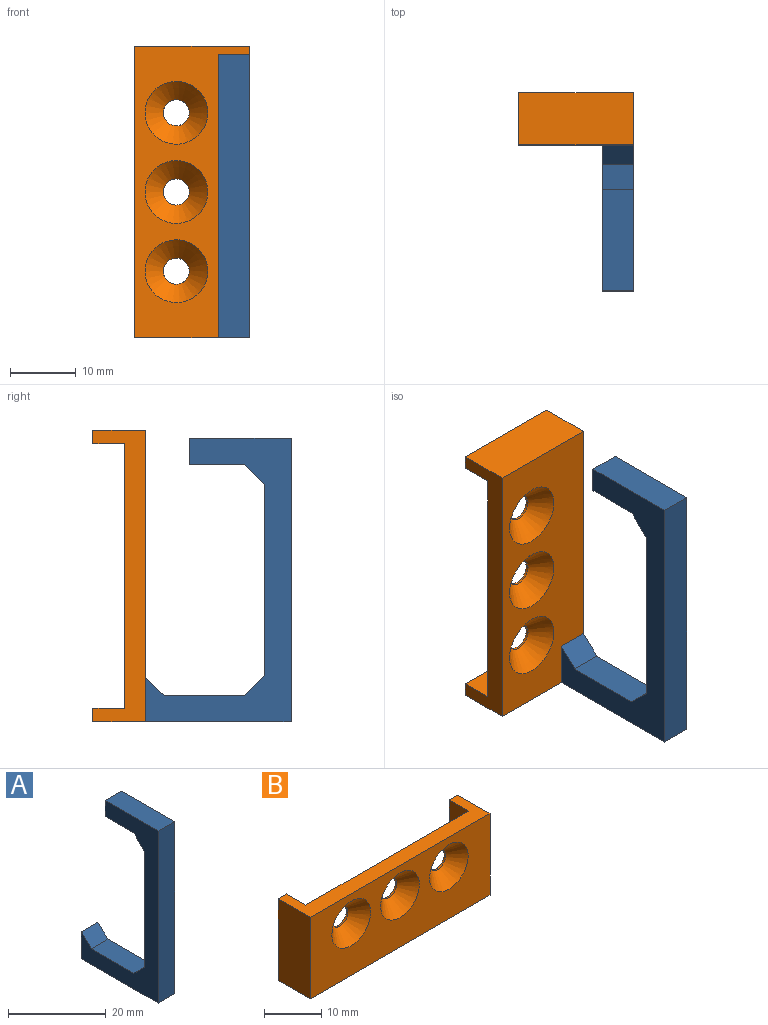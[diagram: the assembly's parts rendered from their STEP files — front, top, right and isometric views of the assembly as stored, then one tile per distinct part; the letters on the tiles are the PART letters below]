
ASSEMBLY  parts=2 mates=1
PART A: 13 faces, bbox 4.8x22.2x43.2 mm
  f0: plane 12.28x4.76mm, normal (0,0,1), area 58.5mm2, adj f1,f9,f10,f12
  f1: plane 4.76x2.93mm, normal (0,-0.69,0.72), area 19.3mm2, adj f0,f2,f9,f10
  f2: plane 6.76x4.76mm, normal (0,1,0), area 32.2mm2, adj f1,f3,f9,f10
  f3: plane 22.23x4.76mm, normal (0,0,-1), area 105.8mm2, adj f2,f4,f9,f10
  f4: plane 43.18x4.76mm, normal (0,-1,0), area 205.6mm2, adj f3,f5,f9,f10
  f5: plane 15.4x4.76mm, normal (0,0,1), area 73.3mm2, adj f4,f6,f9,f10
  f6: plane 4.76x3.97mm, normal (0,1,0), area 18.9mm2, adj f5,f7,f9,f10
  f7: plane 8.38x4.76mm, normal (0,0,-1), area 39.9mm2, adj f6,f9,f10,f11
  f8: plane 29.15x4.76mm, normal (0,1,0), area 138.8mm2, adj f9,f10,f11,f12
  f9: plane 43.18x22.23mm, normal (1,0,0), area 302.6mm2, adj f0,f1,f2,f3,f4,f5,f6,f7
  f10: plane 43.18x22.23mm, normal (-1,0,0), area 302.6mm2, adj f0,f1,f2,f3,f4,f5,f6,f7
  f11: plane 4.76x3.05mm, normal (0,0.71,-0.71), area 20.5mm2, adj f7,f8,f9,f10
  f12: plane 4.76x3.05mm, normal (0,0.71,0.71), area 20.5mm2, adj f0,f8,f9,f10
PART B: 16 faces, bbox 44.5x7.9x17.5 mm
  f0: plane 40.22x17.46mm, normal (0,1,0), area 665.2mm2, adj f1,f7,f8,f9,f10,f11,f12
  f1: plane 17.46x4.76mm, normal (1,0,0), area 83.2mm2, adj f0,f2,f8,f9
  f2: plane 17.46x2.12mm, normal (0,1,0), area 37mm2, adj f1,f3,f8,f9
  f3: plane 17.46x7.94mm, normal (-1,0,0), area 138.6mm2, adj f2,f4,f8,f9
  f4: plane 44.45x17.46mm, normal (0,-1,0), area 561mm2, adj f3,f5,f8,f9,f13,f14,f15
  f5: plane 17.46x7.94mm, normal (1,0,0), area 138.6mm2, adj f4,f6,f8,f9
  f6: plane 17.46x2.12mm, normal (0,1,0), area 37mm2, adj f5,f7,f8,f9
  f7: plane 17.46x4.76mm, normal (-1,0,0), area 83.2mm2, adj f0,f6,f8,f9
  f8: plane 44.45x7.94mm, normal (0,0,-1), area 161.3mm2, adj f0,f1,f2,f3,f4,f5,f6,f7
  f9: plane 44.45x7.94mm, normal (0,0,1), area 161.3mm2, adj f0,f1,f2,f3,f4,f5,f6,f7
  f10: cylinder r=1.98mm len=3.97mm, axis (0,-1,0), area 4.8mm2, adj f0,f13
  f11: cylinder r=1.98mm len=3.97mm, axis (0,-1,0), area 4.8mm2, adj f0,f14
  f12: cylinder r=1.98mm len=3.97mm, axis (0,-1,0), area 4.8mm2, adj f0,f15
  f13: cone r=1.98mm half-angle=45deg, axis (0,-1,0), area 83.9mm2, adj f4,f10
  f14: cone r=1.98mm half-angle=45deg, axis (0,-1,0), area 83.9mm2, adj f4,f11
  f15: cone r=1.98mm half-angle=45deg, axis (0,-1,0), area 83.9mm2, adj f4,f12
PLACE A t=(-0.88,-3.74,-7.15)mm
PLACE B rot(axis=(0,-1,0),90deg) t=(-18.35,-3.74,15.08)mm
MATE revolute B.f4 <-> A.f2  axis (0,1,0) through (-18.35,18.48,-7.15)mm
